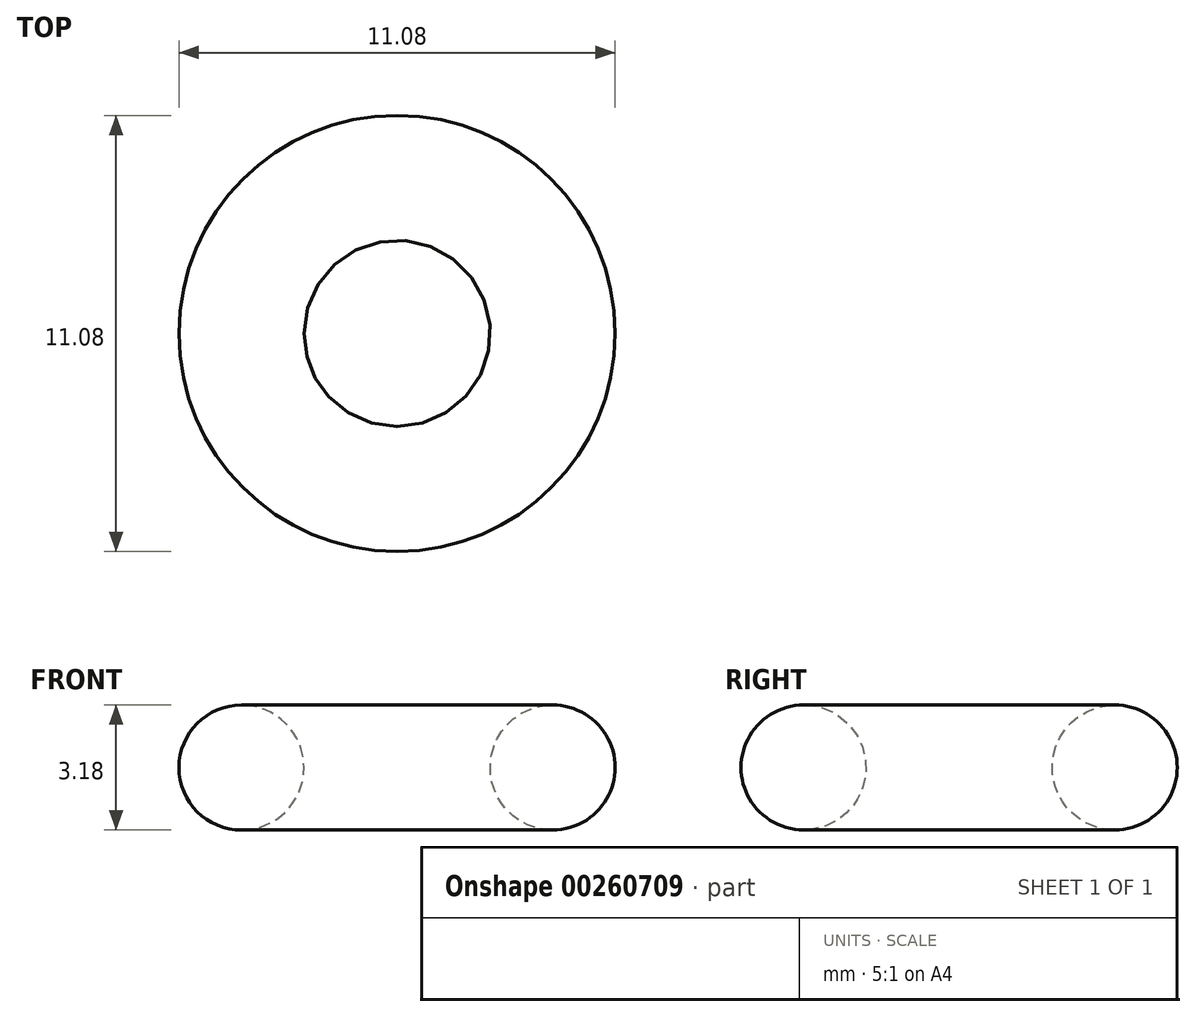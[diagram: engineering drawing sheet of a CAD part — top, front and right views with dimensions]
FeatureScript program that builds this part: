
annotation { "Feature Type Name" : "Feature", "Feature Type Description" : "" }
export const myFeature = defineFeature(function(context is Context, id is Id, definition is map)
    precondition{}
    {
        {
            var Q0;
            Q0=qCreatedBy(makeId("Front.planeOp"),FACE);
            var sketch = newSketch(context, id + "F0", { "sketchPlane" : qUnion([Q0])});
            skLineSegment(sketch, "E0", {"start": v(0, 18.72) * mm, "end": v(0, 39.85) * mm});
            skCircle(sketch, "E1", {"center": v(3.95, 25.55) * mm, "radius": 1.59 * mm});
            skSolve(sketch);
        }
        {
            var Q0;
            Q0 = qSketchRegion(id + "F0", true);
            var Q1;
            Q1=sQuery(id+"F0.wireOp",EDGE,"E0");
            revolve(context, id + "F1", {"entities" : qUnion([Q0]), "axis" : qUnion([Q1]), "revolveType" : RevolveType.FULL});
        }
    });
